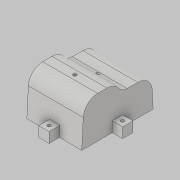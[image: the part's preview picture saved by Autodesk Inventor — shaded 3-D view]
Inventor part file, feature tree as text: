
AUTODESK INVENTOR PART (.ipt)
format: ipt  version: 2019 (Build 230136000, 136)  size: 352,256 bytes
history: native  units: mm
features: extrude x5, fillet x5, sketch x4, other x3, shell x1, plane x1, boolean_combine x1, delete_face x1
ambient origin geometry x8: Origin, YZ Plane, XZ Plane, XY Plane, X Axis, Y Axis, Z Axis, Center Point
bodies: Solid2 (feature_tree)
feature tree (21):
  other  "Sólido1"
  sketch  "Boceto1"  dims[d0=50.0mm d1=30.0mm]
  extrude  "Extrusión1"  Depth=30.0mm
  extrude  "Extrusión2"  Depth=10.0mm
  other  "Cara para el ángulo de desmoldeo2"
  other  "Cara para el ángulo de desmoldeo3"
  fillet  "Empalme1"  Radius=25.0mm
  fillet  "Empalme2"  Radius=70.0mm
  fillet  "Empalme3"  Radius=25.0mm
  fillet  "Empalme4"  Radius=3.0mm
  fillet  "Empalme5"  Radius=6.0mm
  shell  "Vaciado1"  Thickness=6.0mm
  plane  "Work Plane1"
  extrude  "Extrusion3"  Depth=1.0mm
  boolean_combine  "Combine1"
  delete_face  "Delete Face1"
  extrude  "Extrusion4"  Depth=10.0mm
  extrude  "Extrusion5"  Depth=10.0mm
  sketch  "Sketch2"  dims[d2=10.0mm d3=10.0mm d4=25.0mm d5=70.0mm d6=0.0mm d7=25.0mm d8=0.0mm d9=3.0mm d10=6.0mm d11=6.0mm]
  sketch  "Sketch3"  dims[d12=3.0mm d13=1.0mm]
  sketch  "Sketch4"  dims[d15=6.0mm d16=0.523599mm d17=0.523599mm d18=15.0mm d19=15.0mm d21=180.0deg d23=0.0mm d24=80.0mm d25=0.0mm d26=15.0mm d27=30.0mm d28=30.0mm d29=15.0mm d30=15.0mm d31=30.0mm d32=30.0mm d33=5.0mm d34=7.5mm d35=5.0mm d36=7.5mm d37=5.0mm d38=7.5mm d39=5.0mm d40=7.5mm d41=15.0mm d42=0.0mm d43=5.0mm d44=5.0mm d45=15.0mm d46=40.0mm d47=10.0mm d48=0.0mm]
